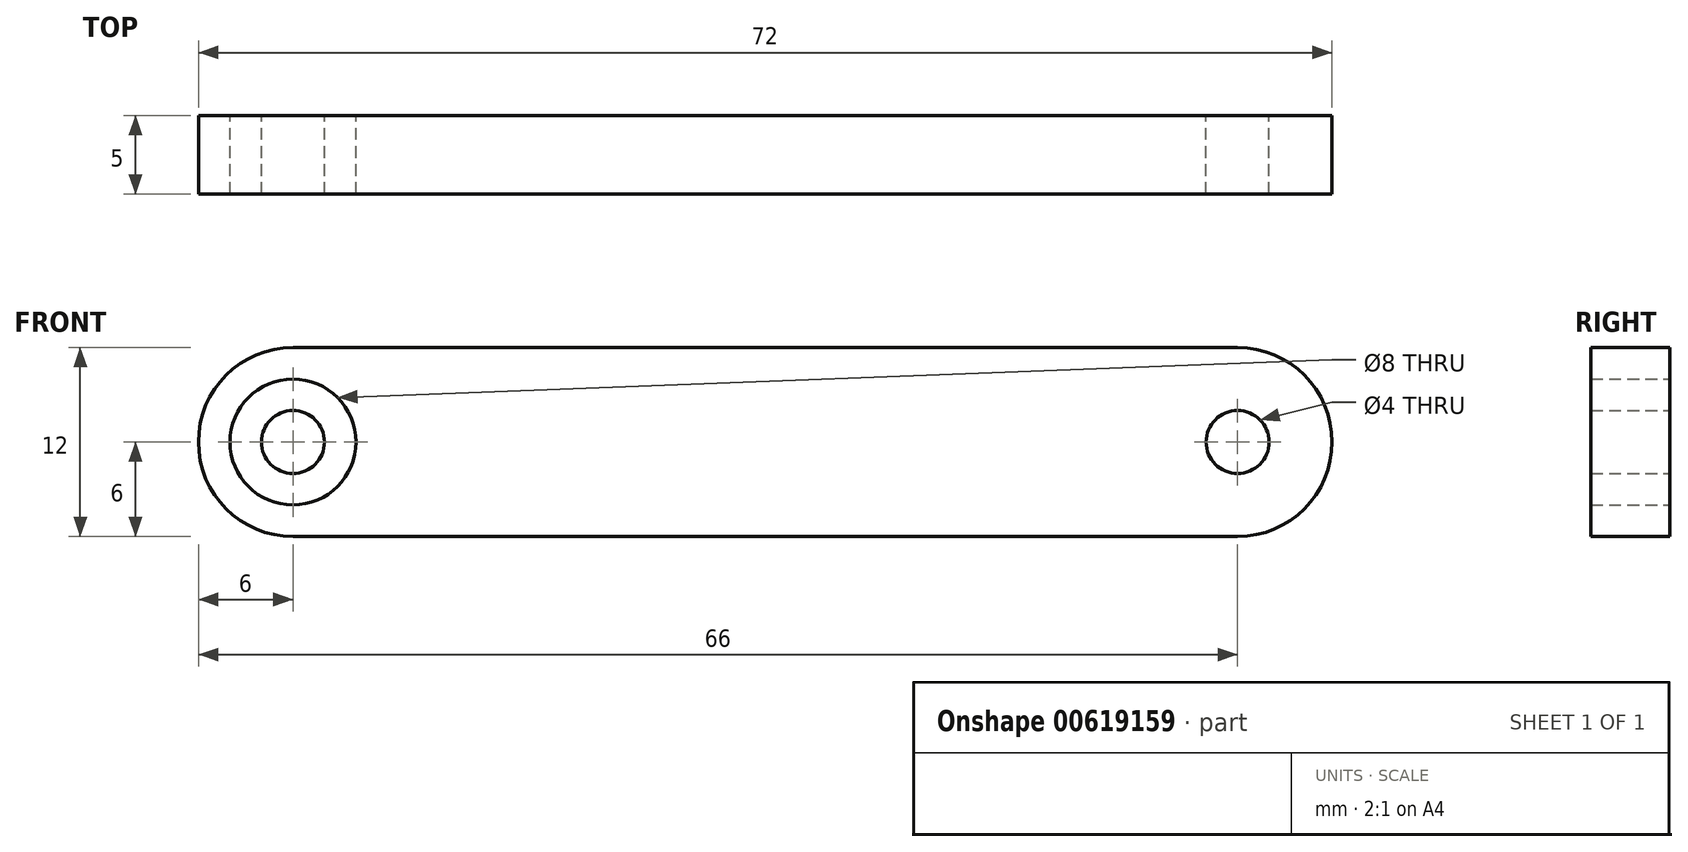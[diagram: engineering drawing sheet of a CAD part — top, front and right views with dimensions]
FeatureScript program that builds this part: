
annotation { "Feature Type Name" : "Feature", "Feature Type Description" : "" }
export const myFeature = defineFeature(function(context is Context, id is Id, definition is map)
    precondition{}
    {
        {
            var Q0;
            Q0=qCreatedBy(makeId("Front.planeOp"),FACE);
            var sketch = newSketch(context, id + "F0", { "sketchPlane" : qUnion([Q0])});
            skLineSegment(sketch, "E0", {"start": v(0, 9.05) * mm, "end": v(0, -10.2) * mm, "construction": true});
            skCircle(sketch, "E1", {"center": v(-30, 0) * mm, "radius": 2 * mm});
            skCircle(sketch, "E2", {"center": v(-30, 0) * mm, "radius": 4 * mm});
            skArc(sketch, "E3", {"start": v(-30, 6) * mm, "mid": v(-36, 0) * mm, "end": v(-30, -6) * mm});
            skLineSegment(sketch, "E4", {"start": v(-30, 6) * mm, "end": v(0, 6) * mm});
            skLineSegment(sketch, "E5", {"start": v(-30, -6) * mm, "end": v(0, -6) * mm});
            skLineSegment(sketch, "E6.MirrorCS", {"start": v(30, 6) * mm, "end": v(0, 6) * mm});
            skLineSegment(sketch, "E7.MirrorCS", {"start": v(30, -6) * mm, "end": v(0, -6) * mm});
            skArc(sketch, "E8.MirrorCS", {"start": v(30, 6) * mm, "mid": v(36, 0) * mm, "end": v(30, -6) * mm});
            skCircle(sketch, "E9.MirrorC", {"center": v(30, 0) * mm, "radius": 2 * mm});
            skCircle(sketch, "E10.MirrorC", {"center": v(30, 0) * mm, "radius": 4 * mm});
            skSolve(sketch);
        }
        {
            var Q0;
            Q0=makeQuery(id+"F0.imprint","IMPRINT",FACE,{"disambiguationData":[TD([[makeQuery(id+"F0.imprint","IMPRINT",EDGE,{"derivedFrom":sQuery(id+"F0.wireOp",EDGE,"E2")}),-1.0]])]});
            var Q1;
            Q1=makeQuery(id+"F0.imprint","IMPRINT",FACE,{"disambiguationData":[TD([[makeQuery(id+"F0.imprint","IMPRINT",EDGE,{"derivedFrom":sQuery(id+"F0.wireOp",EDGE,"E1")}),1.0]])]});
            var Q2;
            Q2=makeQuery(id+"F0.imprint","IMPRINT",FACE,{"disambiguationData":[TD([[makeQuery(id+"F0.imprint","IMPRINT",EDGE,{"derivedFrom":sQuery(id+"F0.wireOp",EDGE,"E9.MirrorC")}),-1.0]])]});
            extrude(context, id + "F1", {"entities" : qUnion([Q0, Q1, Q2]), "depth" : 5 * mm, "offsetDistance" : 25 * mm});
        }
    });
